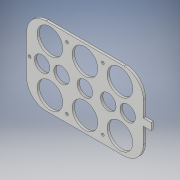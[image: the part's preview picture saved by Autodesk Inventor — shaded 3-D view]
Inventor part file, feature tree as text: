
AUTODESK INVENTOR PART (.ipt)
format: ipt  version: 2017 (Build 210142000, 142)  size: 204,288 bytes
history: native  units: in
note: dims shown in document units (in); Inventor stores cm internally (conversion verified against a paired STEP export)
features: fillet x4, extrude x2, sketch x2
ambient origin geometry x8: Origin, YZ Plane, XZ Plane, XY Plane, X Axis, Y Axis, Z Axis, Center Point
bodies: Body1 (feature_tree)
feature tree (8):
  extrude  "Extrusion5"  Depth=3.937in
  extrude  "Extrusion6"  Depth=0.9843in
  fillet  "Fillet9"  Radius=1.2992in
  fillet  "Fillet10"  Radius=1.2992in
  fillet  "Fillet11"  Radius=1.2992in
  fillet  "Fillet12"  Radius=1.2992in
  sketch  "Sketch1"  dims[d0=5.9055in d1=3.937in]
  sketch  "Sketch4"  dims[d2=1.2992in d3=1.2992in d5=1.2992in d6=1.2992in d8=1.2992in d9=1.2992in d10=0.7874in d11=0.7874in d12=0.7874in d13=1.1811in d14=1.1811in d15=2.9528in d16=1.1811in d17=2.9528in d18=1.1811in d19=0.7874in d20=0.7874in d21=0.7874in d22=0.7874in d23=0.7874in d25=0.7874in d26=0.7874in d27=0.7874in d28=0.7874in d29=0.7874in d30=0.9843in d31=0.9843in d32=1.9685in d33=1.9685in d34=1.9685in d35=1.9685in d36=1.9685in d37=2.9528in d56=0.1378in d57=0.1378in d58=0.1378in d59=0.1378in d60=0.3937in d61=0.3937in d62=0.3937in d63=0.3937in d64=2.0472in d65=2.0472in d66=2.0472in d67=2.0472in d74=0.1378in d75=0.1575in d76=1.9685in d77=0.1181in d78=0.0in d79=0.3543in d80=1.7913in d81=0.3937in d82=0.0in d83=0.9843in d84=0.9843in d85=0.9843in d86=0.9843in]
